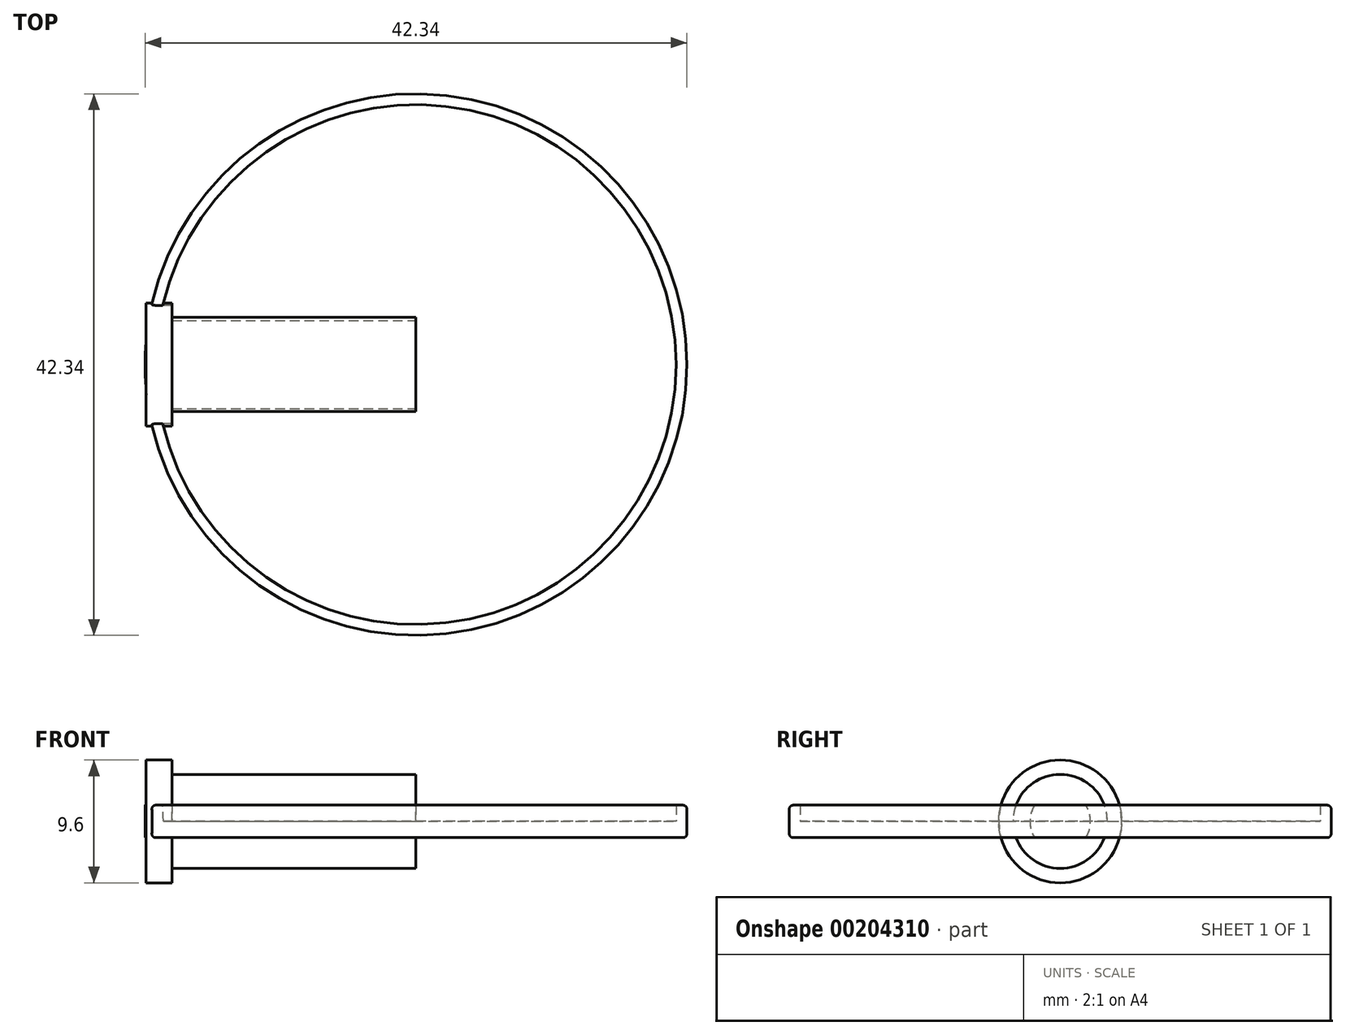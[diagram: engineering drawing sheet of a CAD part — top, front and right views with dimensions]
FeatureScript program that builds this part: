
annotation { "Feature Type Name" : "Feature", "Feature Type Description" : "" }
export const myFeature = defineFeature(function(context is Context, id is Id, definition is map)
    precondition{}
    {
        {
            var Q0;
            Q0=qCreatedBy(makeId("Top.planeOp"),FACE);
            var sketch = newSketch(context, id + "F0", { "sketchPlane" : qUnion([Q0])});
            skArc(sketch, "E0", {"start": v(20.28, 0) * mm, "mid": v(0, 20.28) * mm, "end": v(-20.28, 0) * mm});
            skLineSegment(sketch, "E1", {"start": v(-20.28, 0) * mm, "end": v(20.28, 0) * mm});
            skSolve(sketch);
        }
        {
            var Q0;
            Q0=makeQuery(id+"F0.imprint","IMPRINT",FACE,{"disambiguationData":[TD([[makeQuery(id+"F0.imprint","IMPRINT",EDGE,{"derivedFrom":sQuery(id+"F0.wireOp",EDGE,"E0")}),1.0]])]});
            var Q1;
            Q1=sQuery(id+"F0.wireOp",EDGE,"E0");
            var Q2;
            Q2=sQuery(id+"F0.wireOp",EDGE,"E1");
            revolve(context, id + "F1", {"bodyType" : ToolBodyType.SURFACE, "entities" : qUnion([Q0]), "surfaceEntities" : qUnion([Q1]), "axis" : qUnion([Q2]), "revolveType" : RevolveType.FULL});
        }
        {
            var Q0;
            Q0=qCreatedBy(makeId("Right.planeOp"),FACE);
            var sketch = newSketch(context, id + "F2", { "sketchPlane" : qUnion([Q0])});
            skCircle(sketch, "E2", {"center": v(0, 0) * mm, "radius": 3.68 * mm});
            skSolve(sketch);
        }
        {
            var Q0;
            Q0 = qSketchRegion(id + "F2", true);
            extrude(context, id + "F3", {"entities" : qUnion([Q0]), "oppositeDirection" : true, "depth" : 20.32 * mm});
        }
        {
            var Q0;
            Q0=makeQuery(id+"F3.opExtrude","CAP_FACE",FACE,{"disambiguationData":[OSD([sQuery(id+"F2.wireOp",EDGE,"E2")])],"isStart":false});
            var sketch = newSketch(context, id + "F4", { "sketchPlane" : qUnion([Q0])});
            skCircle(sketch, "E3", {"center": v(0, 0) * mm, "radius": 4.8 * mm});
            skSolve(sketch);
        }
        {
            var Q0;
            Q0=makeQuery(id+"F4.imprint","IMPRINT",FACE,{"disambiguationData":[TD([[makeQuery(id+"F4.imprint","IMPRINT",EDGE,{"derivedFrom":sQuery(id+"F4.wireOp",EDGE,"E3")}),1.0]])]});
            extrude(context, id + "F5", {"entities" : qUnion([Q0]), "operationType" : NewBodyOperationType.ADD, "oppositeDirection" : true, "depth" : 1.27 * mm});
        }
        {
            var Q0;
            {var subQ0=sQuery(id+"F2.wireOp",EDGE,"E2");Q0=makeQuery(id+"F5.boolean.opBoolean","MERGE",FACE,{"derivedFrom":[makeQuery(id+"F3.opExtrude","CAP_FACE",FACE,{"disambiguationData":[OSD([subQ0])],"isStart":false}),makeQuery(id+"F5.opExtrude","CAP_FACE",FACE,{"disambiguationData":[OSD([subQ0,sQuery(id+"F4.wireOp",EDGE,"E3")])],"isStart":true})]});}
            var sketch = newSketch(context, id + "F6", { "sketchPlane" : qUnion([Q0])});
            skCircle(sketch, "E4", {"center": v(0, 0) * mm, "radius": 2.37 * mm});
            skSolve(sketch);
        }
        {
            var Q0;
            Q0=makeQuery(id+"F6.imprint","IMPRINT",FACE,{"disambiguationData":[TD([[makeQuery(id+"F6.imprint","IMPRINT",EDGE,{"derivedFrom":sQuery(id+"F6.wireOp",EDGE,"E4")}),-1.0]])]});
            extrude(context, id + "F7", {"entities" : qUnion([Q0]), "operationType" : NewBodyOperationType.ADD, "depth" : 0.76 * mm});
        }
        {
            var Q0;
            Q0=qCreatedBy(makeId("Top.planeOp"),FACE);
            var sketch = newSketch(context, id + "F8", { "sketchPlane" : qUnion([Q0])});
            skCircle(sketch, "E5", {"center": v(0, 0) * mm, "radius": 21.17 * mm});
            skSolve(sketch);
        }
        {
            var Q0;
            Q0=makeQuery(id+"F8.imprint","IMPRINT",FACE,{"disambiguationData":[TD([[makeQuery(id+"F8.imprint","IMPRINT",EDGE,{"derivedFrom":sQuery(id+"F8.wireOp",EDGE,"E5")}),1.0]])]});
            var sketch = newSketch(context, id + "F9", { "sketchPlane" : qUnion([Q0])});
            skCircle(sketch, "E6", {"center": v(0, 0) * mm, "radius": 20.32 * mm});
            skSolve(sketch);
        }
        {
            var Q0;
            Q0=makeQuery(id+"F9.imprint","IMPRINT",FACE,{"disambiguationData":[TD([[makeQuery(id+"F9.imprint","IMPRINT",EDGE,{"derivedFrom":sQuery(id+"F9.wireOp",EDGE,"E6")}),-1.0]])]});
            extrude(context, id + "F10", {"entities" : qUnion([Q0]), "operationType" : NewBodyOperationType.ADD, "depth" : 1.27 * mm});
        }
        {
            var Q0;
            Q0=makeQuery(id+"F8.imprint","IMPRINT",FACE,{"disambiguationData":[TD([[makeQuery(id+"F8.imprint","IMPRINT",EDGE,{"derivedFrom":sQuery(id+"F8.wireOp",EDGE,"E5")}),1.0]])]});
            extrude(context, id + "F11", {"entities" : qUnion([Q0]), "operationType" : NewBodyOperationType.ADD, "oppositeDirection" : true, "depth" : 1.27 * mm});
        }
        {
            var Q0;
            {var subQ0=sQuery(id+"F4.wireOp",EDGE,"E3");var subQ1=sQuery(id+"F8.wireOp",EDGE,"E5");Q0=makeQuery(id+"F10.boolean.opBoolean","SPLIT",EDGE,{"disambiguationData":[TD([makeQuery(id+"F5.opExtrude","SWEPT_FACE",FACE,{"disambiguationData":[OSD([subQ0])]})])],"derivedFrom":makeQuery(id+"F10.opExtrude","CAP_EDGE",EDGE,{"disambiguationData":[OSD([subQ1])],"isStart":false})});}
            var Q1;
            {var subQ0=sQuery(id+"F8.wireOp",EDGE,"E5");var subQ1=sQuery(id+"F4.wireOp",EDGE,"E3");Q1=makeQuery(id+"F11.boolean.opBoolean","SPLIT",EDGE,{"disambiguationData":[TD([makeQuery(id+"F5.opExtrude","SWEPT_FACE",FACE,{"disambiguationData":[OSD([subQ1])]})])],"derivedFrom":makeQuery(id+"F11.opExtrude","CAP_EDGE",EDGE,{"disambiguationData":[OSD([subQ0])],"isStart":false})});}
            fillet(context, id + "F12", {"entities" : qUnion([Q0, Q1]), "radius" : 0.3 * mm, "tangentPropagation" : true, "allowEdgeOverflow" : false});
        }
        {
            var Q0;
            {var subQ0=sQuery(id+"F2.wireOp",EDGE,"E2");Q0=makeQuery(id+"F11.boolean.opBoolean","SPLIT",FACE,{"disambiguationData":[TD([makeQuery(id+"F11.opExtrude","CAP_FACE",FACE,{"disambiguationData":[OSD([sQuery(id+"F8.wireOp",EDGE,"E5")])],"isStart":false})])],"derivedFrom":makeQuery(id+"F5.boolean.opBoolean","MERGE",FACE,{"derivedFrom":[makeQuery(id+"F3.opExtrude","CAP_FACE",FACE,{"disambiguationData":[OSD([subQ0])],"isStart":false}),makeQuery(id+"F5.opExtrude","CAP_FACE",FACE,{"disambiguationData":[OSD([subQ0,sQuery(id+"F4.wireOp",EDGE,"E3")])],"isStart":true})]})});}
            var Q1;
            {var subQ0=sQuery(id+"F9.wireOp",EDGE,"E6");var subQ2=sQuery(id+"F2.wireOp",EDGE,"E2");Q1=makeQuery(id+"F11.boolean.opBoolean","SPLIT",FACE,{"disambiguationData":[TD([makeQuery(id+"F10.opExtrude","SWEPT_FACE",FACE,{"disambiguationData":[OSD([subQ0])]})])],"derivedFrom":makeQuery(id+"F5.boolean.opBoolean","MERGE",FACE,{"derivedFrom":[makeQuery(id+"F3.opExtrude","CAP_FACE",FACE,{"disambiguationData":[OSD([subQ2])],"isStart":false}),makeQuery(id+"F5.opExtrude","CAP_FACE",FACE,{"disambiguationData":[OSD([subQ2,sQuery(id+"F4.wireOp",EDGE,"E3")])],"isStart":true})]})});}
            extrude(context, id + "F13", {"entities" : qUnion([Q0, Q1]), "operationType" : NewBodyOperationType.ADD, "depth" : 0.76 * mm});
        }
    });
